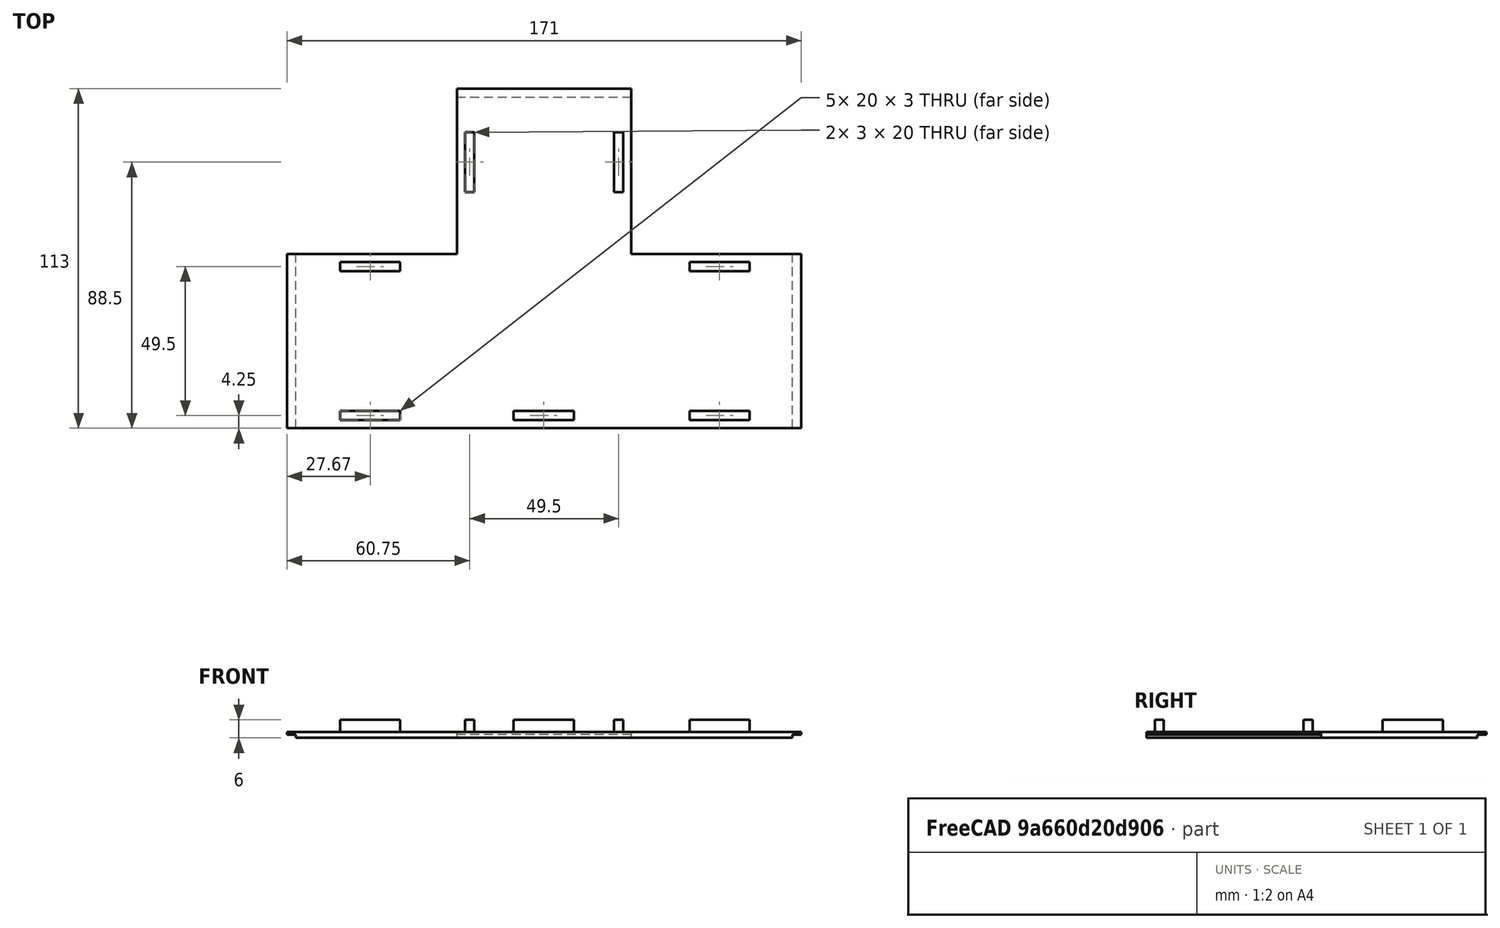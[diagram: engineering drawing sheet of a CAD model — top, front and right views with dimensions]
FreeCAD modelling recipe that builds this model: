
FCSTD DOCUMENT  (FreeCAD 0.21R33694 (Git))
Label: maze_cover_B_v3
License: All rights reserved
LicenseURL: https://en.wikipedia.org/wiki/All_rights_reserved
objects: Part::Box×12, Part::MultiFuse×1
note: 13 computed .brp shape members not serialized (recipe doc carries the construction recipe); baked Part::Feature solids carry a one-line shape summary decoded from their .brp

FEATURE [Part::Box] Box  label="Cube"
  AttacherType = Attacher::AttachEngine3D
  Height = 2
  Length = 165
  Placement = pos=(4,0,0) rot=(0,0,1;0rad)
  Width = 58
FEATURE [Part::Box] Box001  label="Cube001"
  AttacherType = Attacher::AttachEngine3D
  Height = 2
  Length = 110
  Placement = pos=(115.5,0,0) rot=(0,0,1;1.5708rad)
  Width = 58
FEATURE [Part::Box] Box002  label="Cube002"
  AttacherType = Attacher::AttachEngine3D
  Height = 6
  Length = 20
  Placement = pos=(18.67,2.75,0) rot=(0,0,1;0rad)
  Width = 3
FEATURE [Part::Box] Box003  label="Cube003"
  AttacherType = Attacher::AttachEngine3D
  Height = 6
  Length = 20
  Placement = pos=(76.34,2.75,0) rot=(0,0,1;0rad)
  Width = 3
FEATURE [Part::Box] Box004  label="Cube004"
  AttacherType = Attacher::AttachEngine3D
  Height = 6
  Length = 20
  Placement = pos=(134.83,2.75,0) rot=(0,0,1;0rad)
  Width = 3
FEATURE [Part::Box] Box005  label="Cube005"
  AttacherType = Attacher::AttachEngine3D
  Height = 6
  Length = 20
  Placement = pos=(18.67,52.25,0) rot=(0,0,1;0rad)
  Width = 3
FEATURE [Part::Box] Box006  label="Cube006"
  AttacherType = Attacher::AttachEngine3D
  Height = 6
  Length = 20
  Placement = pos=(134.83,52.25,0) rot=(0,0,1;0rad)
  Width = 3
FEATURE [Part::Box] Box007  label="Cube007"
  AttacherType = Attacher::AttachEngine3D
  Height = 6
  Length = 20
  Placement = pos=(63.25,78.5,0) rot=(0,0,1;1.5708rad)
  Width = 3
FEATURE [Part::Box] Box008  label="Cube008"
  AttacherType = Attacher::AttachEngine3D
  Height = 6
  Length = 20
  Placement = pos=(112.75,78.5,0) rot=(0,0,1;1.5708rad)
  Width = 3
FEATURE [Part::Box] Box009  label="Cube009"
  AttacherType = Attacher::AttachEngine3D
  Height = 1
  Length = 3
  Placement = pos=(1,0,1) rot=(0,0,1;0rad)
  Width = 58
FEATURE [Part::Box] Box010  label="Cube010"
  AttacherType = Attacher::AttachEngine3D
  Height = 1
  Length = 3
  Placement = pos=(169,0,1) rot=(0,0,1;0rad)
  Width = 58
FEATURE [Part::Box] Box011  label="Cube011"
  AttacherType = Attacher::AttachEngine3D
  Height = 1
  Length = 3
  Placement = pos=(115.5,110,1) rot=(0,0,1;1.5708rad)
  Width = 58
FEATURE [Part::MultiFuse] Fusion
  Shapes = -> [Box011,Box010,Box009,Box008,Box007,Box006,Box005,Box004,Box003,Box002,Box001,Box]
